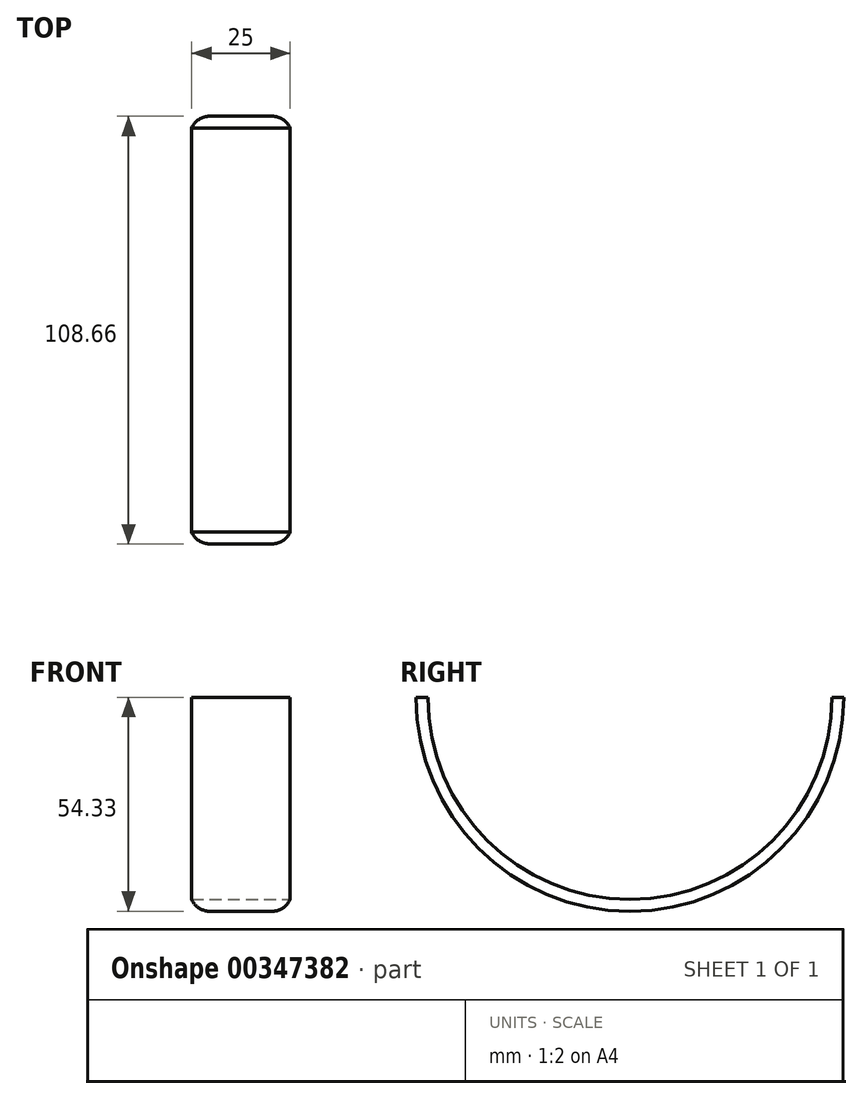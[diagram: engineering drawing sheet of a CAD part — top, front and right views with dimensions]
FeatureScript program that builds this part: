
annotation { "Feature Type Name" : "Feature", "Feature Type Description" : "" }
export const myFeature = defineFeature(function(context is Context, id is Id, definition is map)
    precondition{}
    {
        {
            var Q0;
            Q0=qCreatedBy(makeId("Top.planeOp"),FACE);
            var sketch = newSketch(context, id + "F0", { "sketchPlane" : qUnion([Q0])});
            skLineSegment(sketch, "E0", {"start": v(0, -54.33) * mm, "end": v(-25, -54.33) * mm});
            skLineSegment(sketch, "E1", {"start": v(-25, -51.33) * mm, "end": v(0, -51.33) * mm});
            skLineSegment(sketch, "E2", {"start": v(0, -51.33) * mm, "end": v(0, -54.33) * mm});
            skLineSegment(sketch, "E3", {"start": v(-25, -54.33) * mm, "end": v(-25, -51.33) * mm});
            skLineSegment(sketch, "E4", {"start": v(-66.33, 0) * mm, "end": v(74.33, 0) * mm, "construction": true});
            skSolve(sketch);
        }
        {
            var Q0;
            Q0=sQuery(id+"F0.wireOp",EDGE,"E0");
            var Q1;
            Q1=sQuery(id+"F0.wireOp",EDGE,"E3");
            var Q2;
            Q2=sQuery(id+"F0.wireOp",EDGE,"E1");
            var Q3;
            Q3=sQuery(id+"F0.wireOp",EDGE,"E2");
            var Q4;
            Q4=sQuery(id+"F0.wireOp",EDGE,"E4");
            revolve(context, id + "F1", {"bodyType" : ToolBodyType.SURFACE, "surfaceEntities" : qUnion([Q0, Q1, Q2, Q3]), "axis" : qUnion([Q4]), "revolveType" : RevolveType.ONE_DIRECTION, "angle" : 180 * degree});
        }
        {
            var Q0;
            Q0=makeQuery(id+"F1.opRevolve","SWEPT_FACE",FACE,{"disambiguationData":[OSD([sQuery(id+"F0.wireOp",EDGE,"E0")])]});
            fillet(context, id + "F2", {"entities" : qUnion([Q0]), "radius" : 5 * mm, "tangentPropagation" : true, "allowEdgeOverflow" : false});
        }
    });
